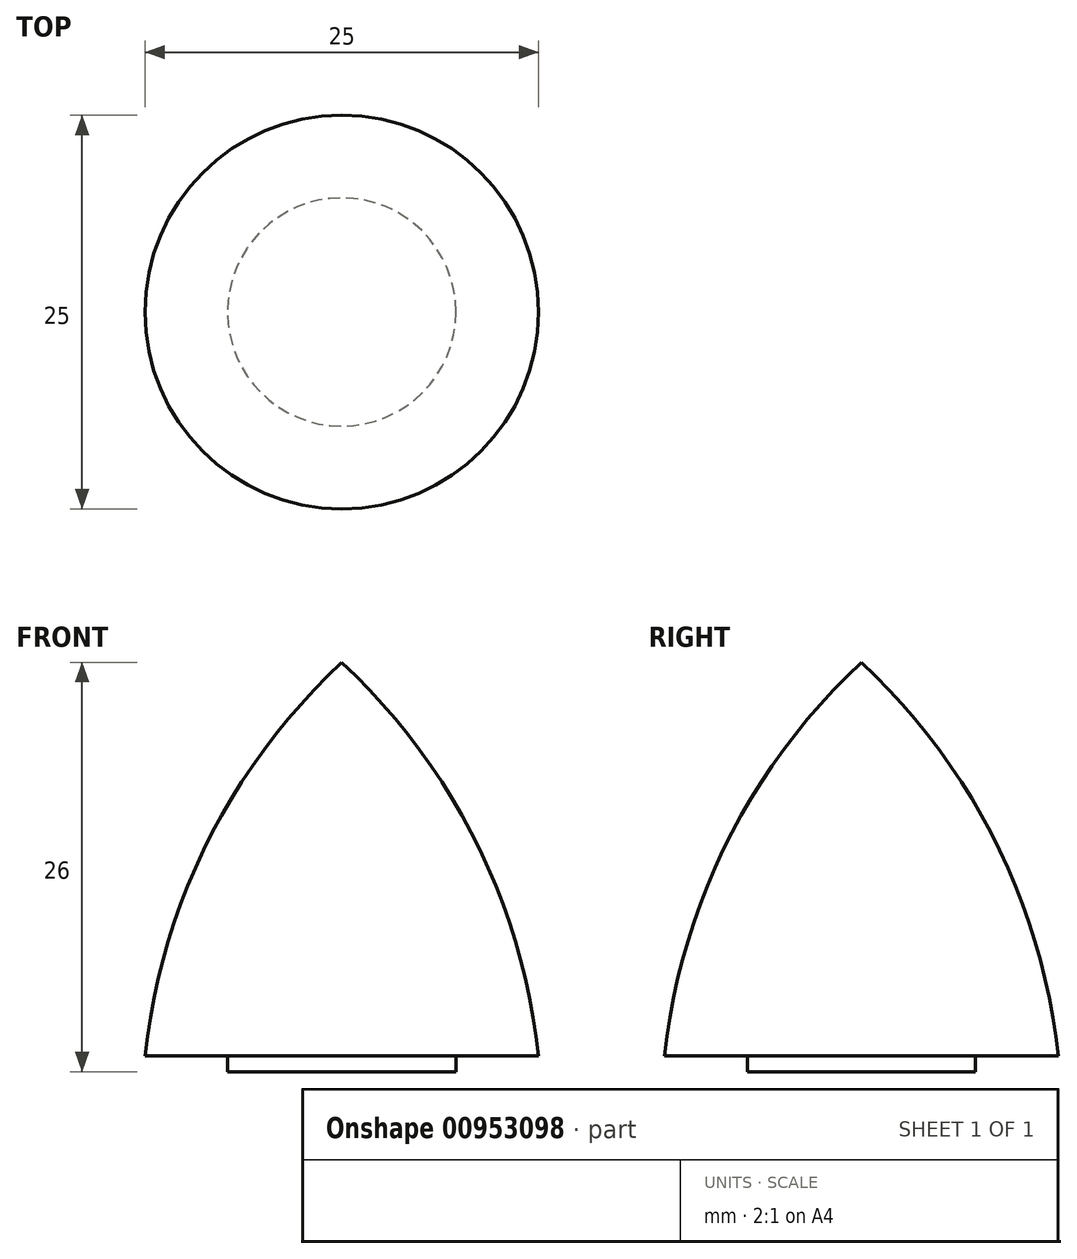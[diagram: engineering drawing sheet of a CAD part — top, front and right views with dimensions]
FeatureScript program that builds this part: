
annotation { "Feature Type Name" : "Feature", "Feature Type Description" : "" }
export const myFeature = defineFeature(function(context is Context, id is Id, definition is map)
    precondition{}
    {
        {
            var Q0;
            Q0=qCreatedBy(makeId("Front.planeOp"),FACE);
            var sketch = newSketch(context, id + "F0", { "sketchPlane" : qUnion([Q0])});
            skLineSegment(sketch, "E0", {"start": v(0, 0) * mm, "end": v(0, -26) * mm});
            skLineSegment(sketch, "E1", {"start": v(0, -26) * mm, "end": v(-7.25, -26) * mm});
            skLineSegment(sketch, "E2", {"start": v(-7.25, -26) * mm, "end": v(-7.25, -25) * mm});
            skLineSegment(sketch, "E3", {"start": v(-7.25, -25) * mm, "end": v(-12.5, -25) * mm});
            skArc(sketch, "E4", {"start": v(0, 0) * mm, "mid": v(-8.5, -11.37) * mm, "end": v(-12.5, -25) * mm});
            skLineSegment(sketch, "E5", {"start": v(0, -26) * mm, "end": v(0, -32.54) * mm, "construction": true});
            skSolve(sketch);
        }
        {
            var Q0;
            Q0 = qSketchRegion(id + "F0", true);
            var Q1;
            Q1=sQuery(id+"F0.wireOp",EDGE,"E5");
            revolve(context, id + "F1", {"surfaceOperationType" : NewSurfaceOperationType.NEW, "entities" : qUnion([Q0]), "axis" : qUnion([Q1]), "revolveType" : RevolveType.FULL});
        }
    });
